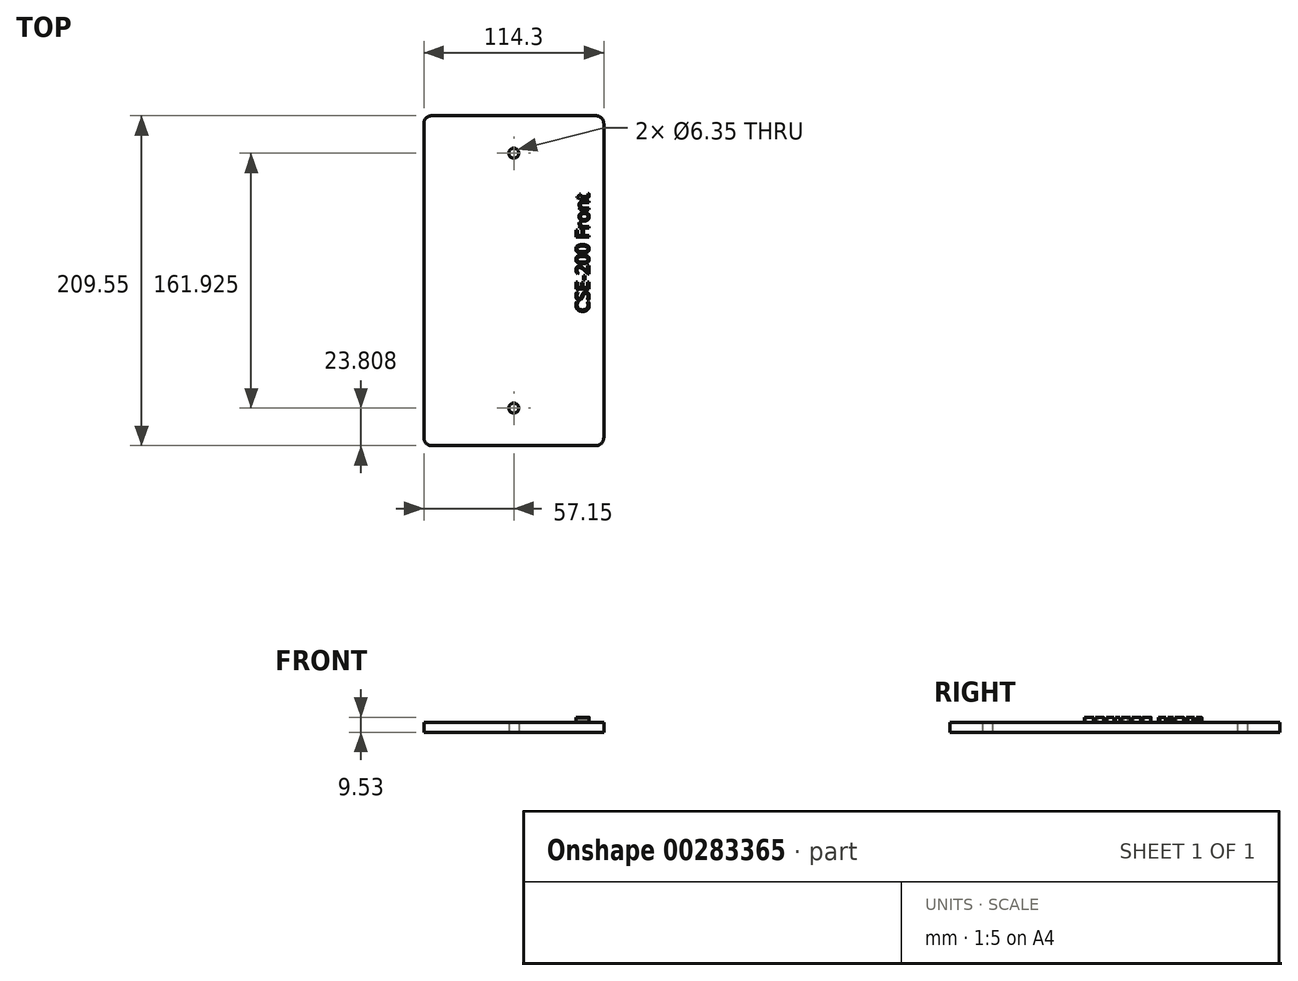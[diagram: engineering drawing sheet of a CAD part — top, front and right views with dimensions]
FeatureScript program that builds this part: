
annotation { "Feature Type Name" : "Feature", "Feature Type Description" : "" }
export const myFeature = defineFeature(function(context is Context, id is Id, definition is map)
    precondition{}
    {
        {
            var Q0;
            Q0=qCreatedBy(makeId("Top.planeOp"),FACE);
            var sketch = newSketch(context, id + "F0", { "sketchPlane" : qUnion([Q0])});
            skLineSegment(sketch, "E0.bottom", {"start": v(-57.15, 121.57) * mm, "end": v(57.15, 121.57) * mm});
            skLineSegment(sketch, "E0.top", {"start": v(-57.15, -87.98) * mm, "end": v(57.15, -87.98) * mm});
            skLineSegment(sketch, "E0.left", {"start": v(-57.15, 121.57) * mm, "end": v(-57.15, -87.98) * mm});
            skLineSegment(sketch, "E0.right", {"start": v(57.15, 121.57) * mm, "end": v(57.15, -87.98) * mm});
            skCircle(sketch, "E1", {"center": v(0, 97.75) * mm, "radius": 3.18 * mm});
            skCircle(sketch, "E2", {"center": v(0, -64.17) * mm, "radius": 3.18 * mm});
            skSolve(sketch);
        }
        {
            var Q0;
            Q0 = qSketchRegion(id + "F0", true);
            extrude(context, id + "F1", {"entities" : qUnion([Q0]), "depth" : 6.35 * mm});
        }
        {
            var Q0;
            Q0=makeQuery(id+"F1.opExtrude","SWEPT_EDGE",EDGE,{"disambiguationData":[OSD([sQuery(id+"F0.wireOp",EDGE,"E0.bottom"),sQuery(id+"F0.wireOp",EDGE,"E0.right")])]});
            var Q1;
            Q1=makeQuery(id+"F1.opExtrude","SWEPT_EDGE",EDGE,{"disambiguationData":[OSD([sQuery(id+"F0.wireOp",EDGE,"E0.bottom"),sQuery(id+"F0.wireOp",EDGE,"E0.left")])]});
            var Q2;
            Q2=makeQuery(id+"F1.opExtrude","SWEPT_EDGE",EDGE,{"disambiguationData":[OSD([sQuery(id+"F0.wireOp",EDGE,"E0.top"),sQuery(id+"F0.wireOp",EDGE,"E0.left")])]});
            var Q3;
            Q3=makeQuery(id+"F1.opExtrude","SWEPT_EDGE",EDGE,{"disambiguationData":[OSD([sQuery(id+"F0.wireOp",EDGE,"E0.top"),sQuery(id+"F0.wireOp",EDGE,"E0.right")])]});
            fillet(context, id + "F2", {"entities" : qUnion([Q0, Q1, Q2, Q3]), "radius" : 5.08 * mm, "tangentPropagation" : true, "allowEdgeOverflow" : false});
        }
        {
            var Q0;
            Q0=makeQuery(id+"F1.opExtrude","CAP_FACE",FACE,{"disambiguationData":[OSD([sQuery(id+"F0.wireOp",EDGE,"E0.bottom"),sQuery(id+"F0.wireOp",EDGE,"E0.top"),sQuery(id+"F0.wireOp",EDGE,"E0.left"),sQuery(id+"F0.wireOp",EDGE,"E0.right"),sQuery(id+"F0.wireOp",EDGE,"E1"),sQuery(id+"F0.wireOp",EDGE,"E2")])],"isStart":false});
            var sketch = newSketch(context, id + "F3", { "sketchPlane" : qUnion([Q0])});
            skText(sketch, "E3", { "text": "CSE-200 Front", "fontName": "OpenSans-Regular.ttf"});
            const initialGuessF3  = {"E3": [0.04779, -0.00346, 0, 1, 0.00835]};
            skSetInitialGuess(sketch, initialGuessF3);
            skSolve(sketch);
        }
        {
            var Q0;
            Q0 = qSketchRegion(id + "F3", true);
            extrude(context, id + "F4", {"entities" : qUnion([Q0]), "operationType" : NewBodyOperationType.ADD, "depth" : 3.17 * mm});
        }
    });
